# Revit family: Electrical_&_Lighting-Teknion-CQAPH_Routes_Shared_Power_Hub-R2018
name_source: partatom
category: Electrical Fixtures
revit_build: Autodesk Revit 2018 (Build: 20190510_1515(x64)
units: mm (PartAtom-declared; Revit-internal decimal feet)

## family parameters
Always vertical = Yes
Cut with Voids When Loaded = No
Maintain Annotation Orientation = No
OmniClass Number = 23.40.20.00
OmniClass Title = General Furniture and Specialties
Part Type = Normal
Room Calculation Point = No
Round Connector Dimension = Use Diameter
Shared = Yes
Work Plane-Based = No

## types (1)
- Octet - 8 Power, Under Worksurface Mounting Configuration
    Apparent Load = 0 VA
    Assembly Code = E2020200
    Connector Descripton = Power Connector
    Description = Routes Shared Power Hub, Octet - 8 Power, Under Worksurface Mounting Configuration
    Manufacturer = Teknion
    Manufacturer Fax = 416.661.4586
    Model = CQAPHO8000U___
    Part Number = CQAPH
    Product Documentation Link = https://assets.teknion.com
    Product Line = Routes
    Product Page URL = https://www.teknion.com
    Series = Routes
    Sustainability Data = https://www.teknion.com
    URL = www.teknion.com
    Unit Weight URL = http://www.teknion.com
    Voltage = 120 V
    Warranty = http://www.teknion.com

## geometry (parser evidence)
native form markers: Sweep x3
no freeform markers — native parametric forms only
